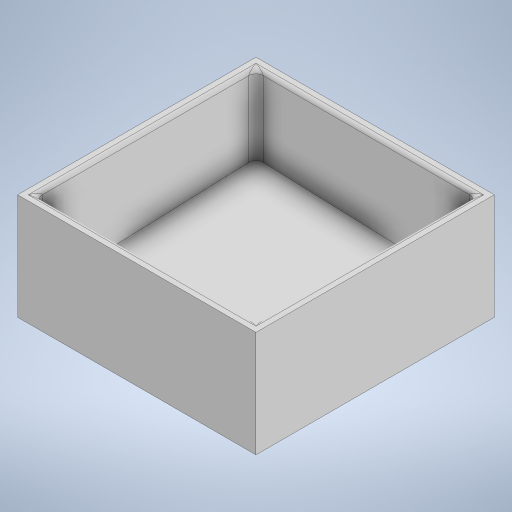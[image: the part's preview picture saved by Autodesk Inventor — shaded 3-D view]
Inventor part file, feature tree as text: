
AUTODESK INVENTOR PART (.ipt)
format: ipt  version: 2024.2 (Build 282272000, 272)  size: 672,768 bytes
history: native  units: in
note: dims shown in document units (in); Inventor stores cm internally (conversion verified against a paired STEP export)
features: projected_geometry x5, extrude x4, sketch x4, plane x2, fillet x2
ambient origin geometry x8: Origin, YZ Plane, XZ Plane, XY Plane, X Axis, Y Axis, Z Axis, Center Point
bodies: Solid1 (feature_tree)
feature tree (17):
  extrude  "Extrusion1"  Depth=3.37in
  plane  "Work Plane3"
  sketch  "Sketch4"  dims[d2=0.125in d3=0.125in d4=0.125in]
  extrude  "Extrusion2"  Depth=0.125in
  fillet  "Fillet1"  Radius=0.125in
  plane  "Work Plane4"
  extrude  "Extrusion3"  Depth=1.5in TaperAngle=0.0deg
  extrude  "Extrusion4"  Depth=0.4in
  fillet  "Fillet2"  [1 undecoded]
  sketch  "Sketch1"  dims[d0=3.37in d1=3.37in]
  projected_geometry  "Projected Loop1"
  projected_geometry  "Projected Loop2"
  sketch  "Sketch5"  dims[d5=0.125in d6=1.5in d7=0.0in]
  projected_geometry  "Projected Loop3"
  sketch  "Sketch6"  dims[d34=45.0deg d35=0.4in d36=0.0in d37=0.0in d38=0.05in d39=-0.29in d40=0.5in d41=0.5in d42=0.318in d43=0.5in d44=0.5in d45=0.318in d46=0.189in d47=0.0in d48=0.15in d49=1.2162in d50=0.14in d51=0.14in d52=0.189in d53=0.0in d54=0.1in]
  projected_geometry  "Projected Loop4"
  projected_geometry  "Projected Loop5"
note: 1 required parameter value undecoded (feature->parameter linkage not recoverable at this tier; creation-order binding heuristic only, values carry confidence <= 0.55)
